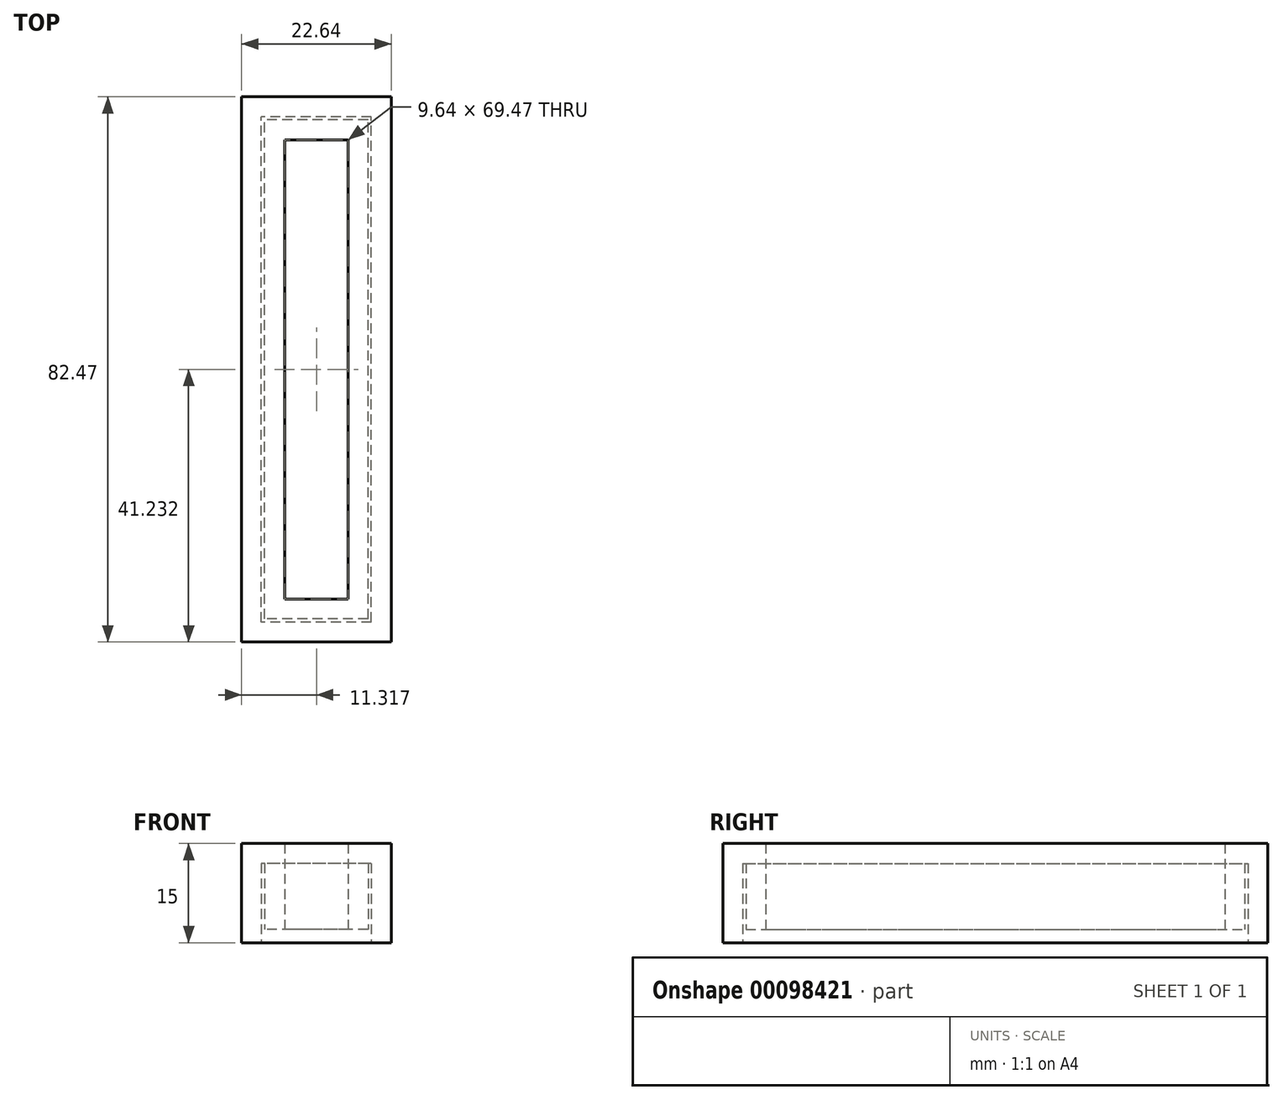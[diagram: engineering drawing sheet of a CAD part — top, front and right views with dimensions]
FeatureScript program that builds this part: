
annotation { "Feature Type Name" : "Feature", "Feature Type Description" : "" }
export const myFeature = defineFeature(function(context is Context, id is Id, definition is map)
    precondition{}
    {
        {
            var Q0;
            Q0=qCreatedBy(makeId("Top.planeOp"),FACE);
            var sketch = newSketch(context, id + "F0", { "sketchPlane" : qUnion([Q0])});
            skLineSegment(sketch, "E0.bottom", {"start": v(38.04, -34.27) * mm, "end": v(21.4, -34.27) * mm});
            skLineSegment(sketch, "E0.top", {"start": v(38.04, 42.2) * mm, "end": v(21.4, 42.2) * mm});
            skLineSegment(sketch, "E0.left", {"start": v(38.04, -34.27) * mm, "end": v(38.04, 42.2) * mm});
            skLineSegment(sketch, "E0.right", {"start": v(21.4, -34.27) * mm, "end": v(21.4, 42.2) * mm});
            skSolve(sketch);
        }
        {
            var Q0;
            Q0 = qSketchRegion(id + "F0", true);
            var Q1;
            Q1=makeQuery(id+"F0.imprint","IMPRINT",FACE,{"disambiguationData":[TD([[makeQuery(id+"F0.imprint","IMPRINT",EDGE,{"derivedFrom":sQuery(id+"F0.wireOp",EDGE,"E0.bottom")}),-1.0]])]});
            extrude(context, id + "F1", {"entities" : qUnion([Q0, Q1]), "depth" : 2 * mm, "offsetDistance" : 25 * mm});
        }
        {
            var Q0;
            Q0=makeQuery(id+"F1.opExtrude","SWEPT_BODY",BODY,{"disambiguationData":[OSD([sQuery(id+"F0.wireOp",EDGE,"E0.bottom"),sQuery(id+"F0.wireOp",EDGE,"E0.top"),sQuery(id+"F0.wireOp",EDGE,"E0.left"),sQuery(id+"F0.wireOp",EDGE,"E0.right")])]});
            transform(context, id + "F2", {"entities" : qUnion([Q0]), "transformType" : TransformType.TRANSLATION_3D, "dx" : 0 * mm, "dy" : 0 * mm, "dz" : 0 * mm, "makeCopy" : true});
        }
        {
            var Q0;
            Q0=makeQuery(id+"F1.opExtrude","CAP_FACE",FACE,{"disambiguationData":[OSD([sQuery(id+"F0.wireOp",EDGE,"E0.bottom"),sQuery(id+"F0.wireOp",EDGE,"E0.top"),sQuery(id+"F0.wireOp",EDGE,"E0.left"),sQuery(id+"F0.wireOp",EDGE,"E0.right")])],"isStart":true});
            var Q1;
            Q1=makeQuery(id+"F1.opExtrude","CAP_FACE",FACE,{"disambiguationData":[OSD([sQuery(id+"F0.wireOp",EDGE,"E0.bottom"),sQuery(id+"F0.wireOp",EDGE,"E0.top"),sQuery(id+"F0.wireOp",EDGE,"E0.left"),sQuery(id+"F0.wireOp",EDGE,"E0.right")])],"isStart":false});
            shell(context, id + "F3", {"entities" : qUnion([Q0, Q1]), "thickness" : .5 * mm});
        }
        {
            var Q0;
            Q0=makeQuery(id+"F1.opExtrude","CAP_FACE",FACE,{"disambiguationData":[OSD([sQuery(id+"F0.wireOp",EDGE,"E0.bottom"),sQuery(id+"F0.wireOp",EDGE,"E0.top"),sQuery(id+"F0.wireOp",EDGE,"E0.left"),sQuery(id+"F0.wireOp",EDGE,"E0.right")])],"isStart":false});
            extrude(context, id + "F4", {"entities" : qUnion([Q0]), "operationType" : NewBodyOperationType.ADD, "depth" : 10 * mm, "offsetDistance" : 25 * mm});
        }
        {
            var Q0;
            Q0=makeQuery(id+"F2.opPattern","COPY",FACE,{"derivedFrom":makeQuery(id+"F1.opExtrude","CAP_FACE",FACE,{"disambiguationData":[OSD([sQuery(id+"F0.wireOp",EDGE,"E0.bottom"),sQuery(id+"F0.wireOp",EDGE,"E0.top"),sQuery(id+"F0.wireOp",EDGE,"E0.left"),sQuery(id+"F0.wireOp",EDGE,"E0.right")])],"isStart":false}),"instanceName":"1"});
            var Q1;
            Q1=makeQuery(id+"F2.opPattern","COPY",FACE,{"derivedFrom":makeQuery(id+"F1.opExtrude","CAP_FACE",FACE,{"disambiguationData":[OSD([sQuery(id+"F0.wireOp",EDGE,"E0.bottom"),sQuery(id+"F0.wireOp",EDGE,"E0.top"),sQuery(id+"F0.wireOp",EDGE,"E0.left"),sQuery(id+"F0.wireOp",EDGE,"E0.right")])],"isStart":true}),"instanceName":"1"});
            shell(context, id + "F5", {"entities" : qUnion([Q0, Q1]), "thickness" : 3 * mm, "oppositeDirection" : true});
        }
    });
